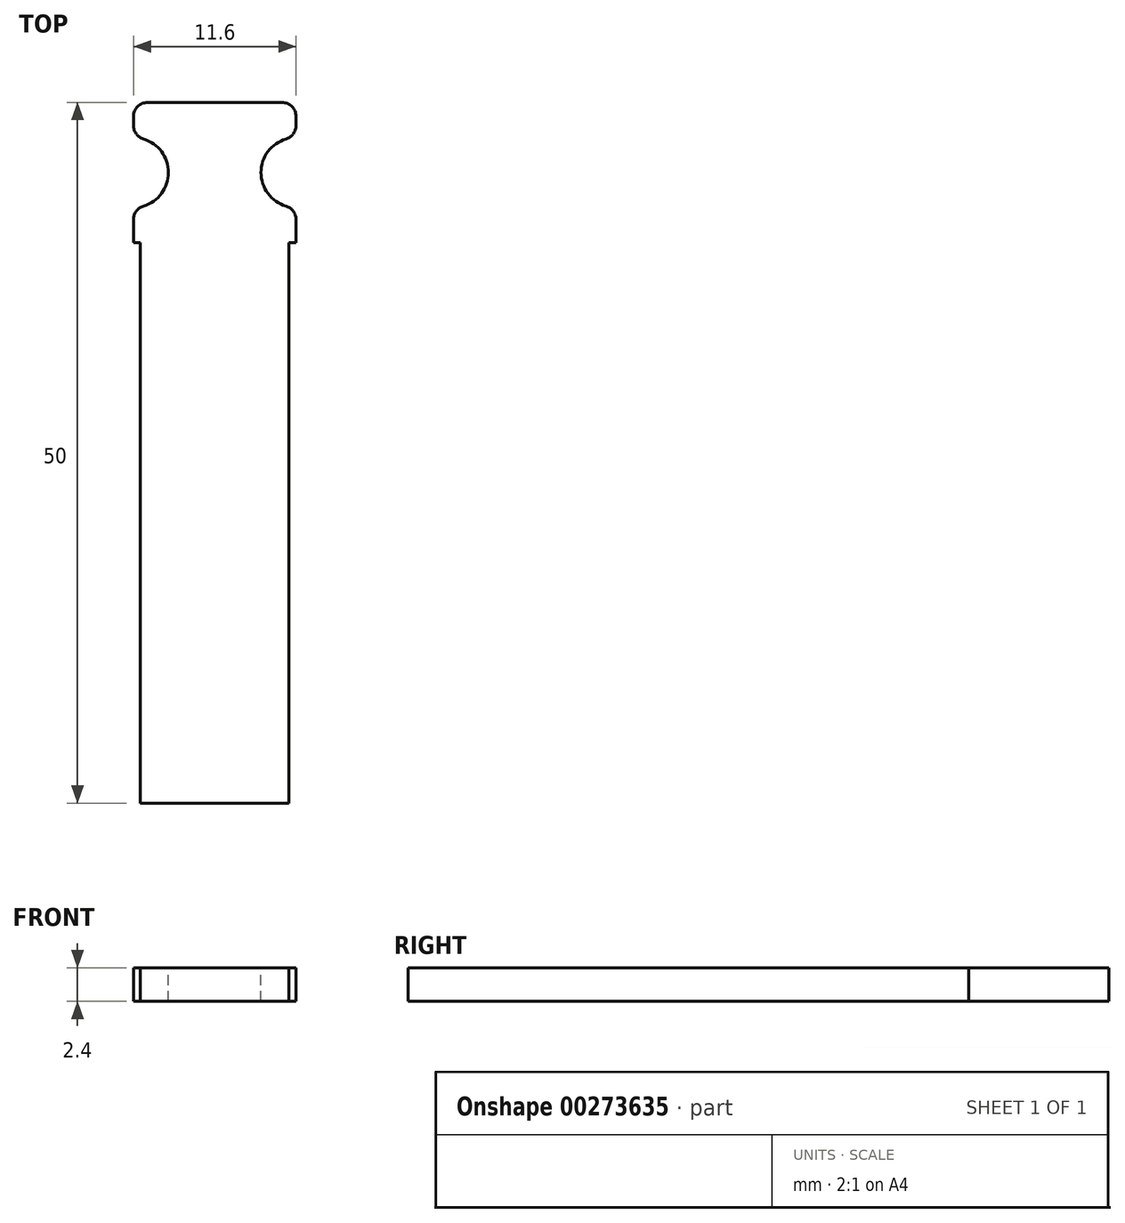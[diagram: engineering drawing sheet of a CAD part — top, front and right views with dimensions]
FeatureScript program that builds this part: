
annotation { "Feature Type Name" : "Feature", "Feature Type Description" : "" }
export const myFeature = defineFeature(function(context is Context, id is Id, definition is map)
    precondition{}
    {
        {
            var Q0;
            Q0=qCreatedBy(makeId("Top.planeOp"),FACE);
            var sketch = newSketch(context, id + "F0", { "sketchPlane" : qUnion([Q0])});
            skLineSegment(sketch, "E0.bottom", {"start": v(-5.8, -25) * mm, "end": v(5.8, -25) * mm});
            skLineSegment(sketch, "E0.top", {"start": v(-5.8, 25) * mm, "end": v(5.8, 25) * mm});
            skLineSegment(sketch, "E0.left", {"start": v(-5.8, -25) * mm, "end": v(-5.8, 25) * mm});
            skLineSegment(sketch, "E0.right", {"start": v(5.8, -25) * mm, "end": v(5.8, 25) * mm});
            skPoint(sketch, "E0.middle", {"position": v(0, 0) * mm});
            skSolve(sketch);
        }
        {
            var Q0;
            Q0 = qSketchRegion(id + "F0", true);
            extrude(context, id + "F1", {"entities" : qUnion([Q0]), "depth" : 2.4 * mm});
        }
        {
            var Q0;
            Q0=makeQuery(id+"F1.opExtrude","CAP_FACE",FACE,{"disambiguationData":[OSD([sQuery(id+"F0.wireOp",EDGE,"E0.bottom"),sQuery(id+"F0.wireOp",EDGE,"E0.top"),sQuery(id+"F0.wireOp",EDGE,"E0.left"),sQuery(id+"F0.wireOp",EDGE,"E0.right")])],"isStart":false});
            var sketch = newSketch(context, id + "F2", { "sketchPlane" : qUnion([Q0])});
            skCircle(sketch, "E1", {"center": v(5.8, 20) * mm, "radius": 2.5 * mm});
            skLineSegment(sketch, "E2.bottom", {"start": v(5.8, 15) * mm, "end": v(5.3, 15) * mm});
            skLineSegment(sketch, "E2.top", {"start": v(5.8, -25) * mm, "end": v(5.3, -25) * mm});
            skLineSegment(sketch, "E2.left", {"start": v(5.8, 15) * mm, "end": v(5.8, -25) * mm});
            skLineSegment(sketch, "E2.right", {"start": v(5.3, 15) * mm, "end": v(5.3, -25) * mm});
            skLineSegment(sketch, "E3", {"start": v(0, 25) * mm, "end": v(0, -25) * mm, "construction": true});
            skCircle(sketch, "E4.MirrorC", {"center": v(-5.8, 20) * mm, "radius": 2.5 * mm});
            skLineSegment(sketch, "E5.MirrorCS", {"start": v(-5.8, 15) * mm, "end": v(-5.3, 15) * mm});
            skLineSegment(sketch, "E6.MirrorCS", {"start": v(-5.3, 15) * mm, "end": v(-5.3, -25) * mm});
            skLineSegment(sketch, "E7.MirrorCS", {"start": v(-5.8, 15) * mm, "end": v(-5.8, -25) * mm});
            skLineSegment(sketch, "E8.MirrorCS", {"start": v(-5.8, -25) * mm, "end": v(-5.3, -25) * mm});
            skSolve(sketch);
        }
        {
            var Q0;
            Q0 = qSketchRegion(id + "F2", true);
            extrude(context, id + "F3", {"entities" : qUnion([Q0]), "operationType" : NewBodyOperationType.REMOVE, "oppositeDirection" : true, "depth" : 25 * mm});
        }
        {
            var Q0;
            Q0=makeQuery(id+"F3.boolean.opBoolean","INTERSECT",EDGE,{"disambiguationData":[OD(0.0)],"derivedFrom":[makeQuery(id+"F1.opExtrude","SWEPT_FACE",FACE,{"disambiguationData":[OSD([sQuery(id+"F0.wireOp",EDGE,"E0.right")])]}),makeQuery(id+"F3.opExtrude","SWEPT_FACE",FACE,{"disambiguationData":[OSD([sQuery(id+"F2.wireOp",EDGE,"E1")])]})]});
            var Q1;
            Q1=makeQuery(id+"F3.boolean.opBoolean","INTERSECT",EDGE,{"disambiguationData":[OD(1.0)],"derivedFrom":[makeQuery(id+"F1.opExtrude","SWEPT_FACE",FACE,{"disambiguationData":[OSD([sQuery(id+"F0.wireOp",EDGE,"E0.right")])]}),makeQuery(id+"F3.opExtrude","SWEPT_FACE",FACE,{"disambiguationData":[OSD([sQuery(id+"F2.wireOp",EDGE,"E1")])]})]});
            var Q2;
            Q2=makeQuery(id+"F3.boolean.opBoolean","INTERSECT",EDGE,{"disambiguationData":[OD(0.0)],"derivedFrom":[makeQuery(id+"F1.opExtrude","SWEPT_FACE",FACE,{"disambiguationData":[OSD([sQuery(id+"F0.wireOp",EDGE,"E0.left")])]}),makeQuery(id+"F3.opExtrude","SWEPT_FACE",FACE,{"disambiguationData":[OSD([sQuery(id+"F2.wireOp",EDGE,"E4.MirrorC")])]})]});
            var Q3;
            Q3=makeQuery(id+"F3.boolean.opBoolean","INTERSECT",EDGE,{"disambiguationData":[OD(1.0)],"derivedFrom":[makeQuery(id+"F1.opExtrude","SWEPT_FACE",FACE,{"disambiguationData":[OSD([sQuery(id+"F0.wireOp",EDGE,"E0.left")])]}),makeQuery(id+"F3.opExtrude","SWEPT_FACE",FACE,{"disambiguationData":[OSD([sQuery(id+"F2.wireOp",EDGE,"E4.MirrorC")])]})]});
            var Q4;
            Q4=makeQuery(id+"F1.opExtrude","SWEPT_EDGE",EDGE,{"disambiguationData":[OSD([sQuery(id+"F0.wireOp",EDGE,"E0.top"),sQuery(id+"F0.wireOp",EDGE,"E0.right")])]});
            var Q5;
            Q5=makeQuery(id+"F1.opExtrude","SWEPT_EDGE",EDGE,{"disambiguationData":[OSD([sQuery(id+"F0.wireOp",EDGE,"E0.top"),sQuery(id+"F0.wireOp",EDGE,"E0.left")])]});
            fillet(context, id + "F4", {"entities" : qUnion([Q0, Q1, Q2, Q3, Q4, Q5]), "radius" : 1 * mm, "tangentPropagation" : true, "allowEdgeOverflow" : false});
        }
    });
